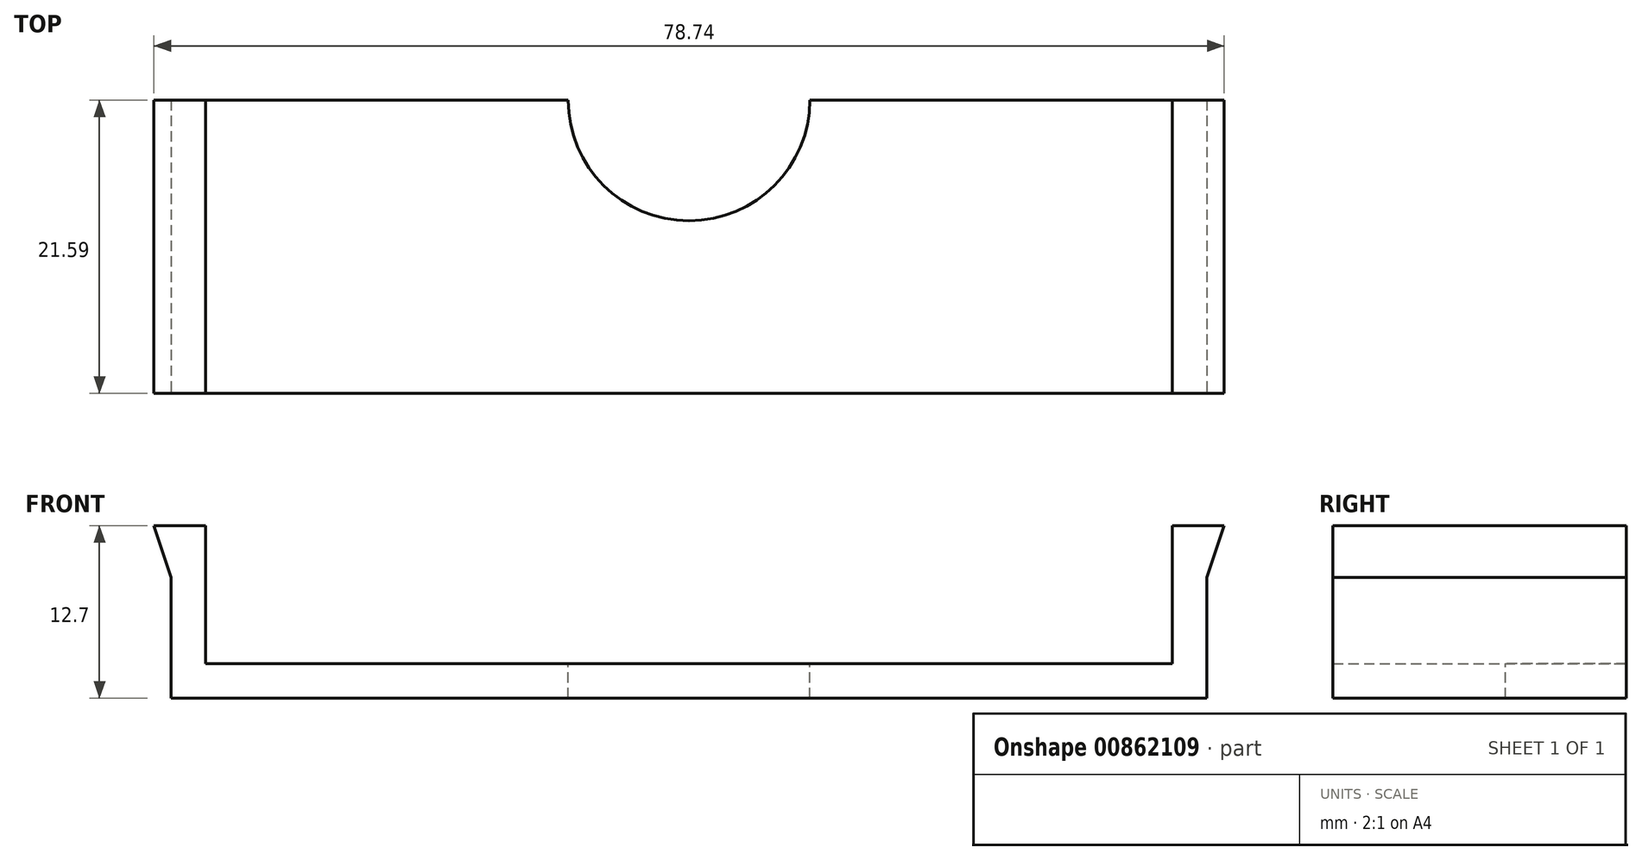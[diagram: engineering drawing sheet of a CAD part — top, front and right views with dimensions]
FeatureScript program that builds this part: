
annotation { "Feature Type Name" : "Feature", "Feature Type Description" : "" }
export const myFeature = defineFeature(function(context is Context, id is Id, definition is map)
    precondition{}
    {
        {
            var Q0;
            Q0=qCreatedBy(makeId("Top.planeOp"),FACE);
            var sketch = newSketch(context, id + "F0", { "sketchPlane" : qUnion([Q0])});
            skLineSegment(sketch, "E0.bottom", {"start": v(0, 0) * mm, "end": v(76.2, 0) * mm});
            skLineSegment(sketch, "E0.top", {"start": v(0, 21.59) * mm, "end": v(76.2, 21.59) * mm});
            skLineSegment(sketch, "E0.left", {"start": v(0, 0) * mm, "end": v(0, 21.59) * mm});
            skLineSegment(sketch, "E0.right", {"start": v(76.2, 0) * mm, "end": v(76.2, 21.59) * mm});
            skSolve(sketch);
        }
        {
            var Q0;
            Q0=makeQuery(id+"F0.imprint","IMPRINT",FACE,{"disambiguationData":[TD([[makeQuery(id+"F0.imprint","IMPRINT",EDGE,{"derivedFrom":sQuery(id+"F0.wireOp",EDGE,"E0.bottom")}),1.0]])]});
            extrude(context, id + "F1", {"entities" : qUnion([Q0]), "depth" : 2.54 * mm, "offsetDistance" : 25.4 * mm});
        }
        {
            var Q0;
            Q0=makeQuery(id+"F1.opExtrude","CAP_FACE",FACE,{"disambiguationData":[OSD([sQuery(id+"F0.wireOp",EDGE,"E0.bottom"),sQuery(id+"F0.wireOp",EDGE,"E0.top"),sQuery(id+"F0.wireOp",EDGE,"E0.left"),sQuery(id+"F0.wireOp",EDGE,"E0.right")])],"isStart":false});
            var sketch = newSketch(context, id + "F2", { "sketchPlane" : qUnion([Q0])});
            skLineSegment(sketch, "E1.bottom", {"start": v(76.2, 21.59) * mm, "end": v(73.66, 21.59) * mm});
            skLineSegment(sketch, "E1.top", {"start": v(76.2, 0) * mm, "end": v(73.66, 0) * mm});
            skLineSegment(sketch, "E1.left", {"start": v(76.2, 21.59) * mm, "end": v(76.2, 0) * mm});
            skLineSegment(sketch, "E1.right", {"start": v(73.66, 21.59) * mm, "end": v(73.66, 0) * mm});
            skLineSegment(sketch, "E2.bottom", {"start": v(0, 0) * mm, "end": v(2.54, 0) * mm});
            skLineSegment(sketch, "E2.top", {"start": v(0, 21.59) * mm, "end": v(2.54, 21.59) * mm});
            skLineSegment(sketch, "E2.left", {"start": v(0, 0) * mm, "end": v(0, 21.59) * mm});
            skLineSegment(sketch, "E2.right", {"start": v(2.54, 0) * mm, "end": v(2.54, 21.59) * mm});
            skSolve(sketch);
        }
        {
            var Q0;
            Q0=makeQuery(id+"F2.imprint","IMPRINT",FACE,{"disambiguationData":[TD([[makeQuery(id+"F2.imprint","IMPRINT",EDGE,{"derivedFrom":sQuery(id+"F2.wireOp",EDGE,"E2.bottom")}),1.0]])]});
            var Q1;
            Q1=makeQuery(id+"F2.imprint","IMPRINT",FACE,{"disambiguationData":[TD([[makeQuery(id+"F2.imprint","IMPRINT",EDGE,{"derivedFrom":sQuery(id+"F2.wireOp",EDGE,"E1.bottom")}),-1.0]])]});
            extrude(context, id + "F3", {"entities" : qUnion([Q0, Q1]), "operationType" : NewBodyOperationType.ADD, "depth" : 10.16 * mm, "offsetDistance" : 25.4 * mm});
        }
        {
            var Q0;
            Q0=makeQuery(id+"F1.opExtrude","CAP_FACE",FACE,{"disambiguationData":[OSD([sQuery(id+"F0.wireOp",EDGE,"E0.bottom"),sQuery(id+"F0.wireOp",EDGE,"E0.top"),sQuery(id+"F0.wireOp",EDGE,"E0.left"),sQuery(id+"F0.wireOp",EDGE,"E0.right")])],"isStart":false});
            var sketch = newSketch(context, id + "F4", { "sketchPlane" : qUnion([Q0])});
            skLineSegment(sketch, "E3", {"start": v(2.54, 10.8) * mm, "end": v(73.66, 10.8) * mm, "construction": true});
            skCircle(sketch, "E4", {"center": v(38.1, 21.59) * mm, "radius": 8.9 * mm});
            skSolve(sketch);
        }
        {
            var Q0;
            Q0=makeQuery(id+"F4.imprint","IMPRINT",FACE,{"disambiguationData":[TD([[makeQuery(id+"F4.imprint","IMPRINT",EDGE,{"derivedFrom":sQuery(id+"F4.wireOp",EDGE,"PgA4HHWj-m7D3-PoWC-p7U9-9KToe9dgFh9g")}),1.0]])]});
            var Q1;
            {var subQ0=sQuery(id+"F4.wireOp",EDGE,"E4");var subQ1=makeQuery(id+"F1.opExtrude","CAP_EDGE",EDGE,{"disambiguationData":[OSD([sQuery(id+"F0.wireOp",EDGE,"E0.top")])],"isStart":false});var subQ2=makeQuery(id+"F4.imprint","INTERSECT",VERTEX,{"disambiguationData":[OD(0.0)],"derivedFrom":[subQ1,subQ0]});Q1=makeQuery(id+"F4.imprint","IMPRINT",FACE,{"disambiguationData":[TD([[makeQuery(id+"F4.imprint","IMPRINT",EDGE,{"disambiguationData":[TD([[subQ2,-1.0]])],"derivedFrom":subQ0}),1.0]])]});}
            var Q2;
            {var subQ0=sQuery(id+"F4.wireOp",EDGE,"E4");var subQ1=makeQuery(id+"F1.opExtrude","CAP_EDGE",EDGE,{"disambiguationData":[OSD([sQuery(id+"F0.wireOp",EDGE,"E0.top")])],"isStart":false});var subQ2=makeQuery(id+"F4.imprint","INTERSECT",VERTEX,{"disambiguationData":[OD(0.0)],"derivedFrom":[subQ1,subQ0]});Q2=makeQuery(id+"F4.imprint","IMPRINT",FACE,{"disambiguationData":[TD([[makeQuery(id+"F4.imprint","IMPRINT",EDGE,{"disambiguationData":[TD([[subQ2,1.0]])],"derivedFrom":subQ0}),1.0]])]});}
            extrude(context, id + "F5", {"entities" : qUnion([Q0, Q1, Q2]), "operationType" : NewBodyOperationType.REMOVE, "oppositeDirection" : true, "depth" : 25.4 * mm, "offsetDistance" : 25.4 * mm});
        }
        {
            var Q0;
            Q0=makeQuery(id+"F3.boolean.opBoolean","MERGE",FACE,{"derivedFrom":[makeQuery(id+"F1.opExtrude","SWEPT_FACE",FACE,{"disambiguationData":[OSD([sQuery(id+"F0.wireOp",EDGE,"E0.bottom")])]}),makeQuery(id+"F3.opExtrude","SWEPT_FACE",FACE,{"disambiguationData":[OSD([sQuery(id+"F2.wireOp",EDGE,"E1.top")])]}),makeQuery(id+"F3.opExtrude","SWEPT_FACE",FACE,{"disambiguationData":[OSD([sQuery(id+"F2.wireOp",EDGE,"E2.bottom")])]})]});
            var sketch = newSketch(context, id + "F6", { "sketchPlane" : qUnion([Q0])});
            skLineSegment(sketch, "E5", {"start": v(0, 12.7) * mm, "end": v(-1.27, 12.7) * mm});
            skLineSegment(sketch, "E6", {"start": v(-1.27, 12.7) * mm, "end": v(0, 8.9) * mm});
            skLineSegment(sketch, "E7", {"start": v(0, 12.7) * mm, "end": v(0, 8.9) * mm});
            skLineSegment(sketch, "E8", {"start": v(76.2, 12.7) * mm, "end": v(77.47, 12.7) * mm});
            skLineSegment(sketch, "E9", {"start": v(77.47, 12.7) * mm, "end": v(76.2, 8.9) * mm});
            skLineSegment(sketch, "E10", {"start": v(76.2, 12.7) * mm, "end": v(76.2, 8.9) * mm});
            skSolve(sketch);
        }
        {
            var Q0;
            Q0=makeQuery(id+"F6.imprint","IMPRINT",FACE,{"disambiguationData":[TD([[makeQuery(id+"F6.imprint","IMPRINT",EDGE,{"derivedFrom":sQuery(id+"F6.wireOp",EDGE,"E5")}),1.0]])]});
            var Q1;
            Q1=makeQuery(id+"F6.imprint","IMPRINT",FACE,{"disambiguationData":[TD([[makeQuery(id+"F6.imprint","IMPRINT",EDGE,{"derivedFrom":sQuery(id+"F6.wireOp",EDGE,"E8")}),-1.0]])]});
            var Q2;
            Q2=makeQuery(id+"F3.boolean.opBoolean","MERGE",FACE,{"derivedFrom":[makeQuery(id+"F1.opExtrude","SWEPT_FACE",FACE,{"disambiguationData":[OSD([sQuery(id+"F0.wireOp",EDGE,"E0.top")])]}),makeQuery(id+"F3.opExtrude","SWEPT_FACE",FACE,{"disambiguationData":[OSD([sQuery(id+"F2.wireOp",EDGE,"E1.bottom")])]}),makeQuery(id+"F3.opExtrude","SWEPT_FACE",FACE,{"disambiguationData":[OSD([sQuery(id+"F2.wireOp",EDGE,"E2.top")])]})]});
            extrude(context, id + "F7", {"entities" : qUnion([Q0, Q1]), "operationType" : NewBodyOperationType.ADD, "endBound" : BoundingType.UP_TO_SURFACE, "oppositeDirection" : true, "depth" : 25.4 * mm, "endBoundEntityFace" : qUnion([Q2]), "offsetDistance" : 25.4 * mm});
        }
    });
